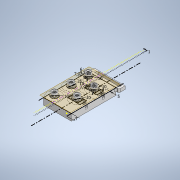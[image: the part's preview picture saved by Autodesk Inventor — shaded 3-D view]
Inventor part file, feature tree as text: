
AUTODESK INVENTOR PART (.ipt)
format: ipt  version: 2022.2 (Build 262287000, 287)  size: 5,227,520 bytes
history: native  units: mm
features: sketch x18, extrude x9, thread x5, revolve x5, helix x5, projected_geometry x4, other x3, plane x2, chamfer x1, reference x1
ambient origin geometry x8: Origin, YZ Plane, XZ Plane, XY Plane, X Axis, Y Axis, Z Axis, Center Point
bodies: Solid1 (feature_tree), Solid7 (feature_tree), Solid8 (feature_tree), Solid9 (feature_tree), Solid10 (feature_tree), Solid11 (feature_tree)
feature tree (53):
  sketch  "Sketch1"  dims[d0=20.0mm d1=7.92mm]
  extrude  "Base Plate"  Depth=7.92mm
  extrude  "Bearing Washer"  Depth=10.0mm
  extrude  "Straightening Pins"  Depth=1.0mm
  extrude  "Base Rails"  Depth=4.0mm
  extrude  "Slider Rails"  Depth=5.0mm
  extrude  "Nut Cavities"  Depth=10.0mm
  extrude  "Tightening Holes"  Depth=10.0mm
  extrude  "Spring Mount"  Depth=10.0mm
  chamfer  "Chamfer1"  Distance=10.0mm
  thread  "Thread1"  [1 undecoded]
  thread  "Thread2"  [1 undecoded]
  thread  "Thread3"  [1 undecoded]
  thread  "Thread4"  [1 undecoded]
  thread  "Thread5"  [1 undecoded]
  revolve  "Revolution6"  [1 undecoded]
  helix  "Coil6"  [1 undecoded]
  revolve  "Revolution7"  [1 undecoded]
  helix  "Coil7"  [1 undecoded]
  revolve  "Revolution8"  [1 undecoded]
  helix  "Coil8"  [1 undecoded]
  revolve  "Revolution9"  [1 undecoded]
  helix  "Coil9"  [1 undecoded]
  revolve  "Revolution10"  [1 undecoded]
  helix  "Coil10"  [1 undecoded]
  plane  "Work Plane3"
  sketch  "Sketch29"  dims[d188=0.7007mm d189=16.4mm d190=10.0mm d191=0.0mm d192=0.0mm d193=0.0mm d194=0.0mm d195=0.0mm]
  plane  "Work Plane4"
  extrude  "Extrusion13"  Depth=9.599311mm
  sketch  "Sketch30"  dims[d196=9.599311mm d197=0.112058mm d198=0.112058mm d201=0.7mm d203=9.599311mm d205=0.0mm d206=0.7007mm d207=16.4mm d208=10.0mm d209=0.0mm d210=0.0mm d211=0.0mm d212=0.0mm d213=0.0mm d214=9.599311mm d215=0.112058mm d216=0.112058mm d219=0.7mm d221=9.599311mm d223=0.0mm d224=0.7007mm d225=16.4mm d226=10.0mm d227=0.0mm d228=0.0mm d229=0.0mm d230=0.0mm d231=0.0mm d232=9.599311mm d233=0.112058mm d234=0.112058mm d237=0.7mm d239=9.599311mm d241=0.0mm d242=0.7007mm d243=16.4mm d244=10.0mm d245=0.0mm d246=0.0mm d247=0.0mm d248=0.0mm d249=0.0mm d250=9.599311mm d251=0.112058mm d252=0.112058mm d255=0.7mm d257=9.599311mm d259=0.0mm d260=0.7007mm d261=16.4mm d262=10.0mm d263=0.0mm d264=0.0mm d265=0.0mm d266=0.0mm d267=0.0mm d268=0.0mm d269=0.0mm d272=2.0mm d273=4.0mm]
  sketch  "Sketch2"  dims[d2=4.2mm d3=30.0mm d5=25.0mm d6=10.0mm d8=10.0mm]
  projected_geometry  "Projected Loop1"
  projected_geometry  "Projected Loop2"
  projected_geometry  "Projected Loop3"
  projected_geometry  "Projected Loop4"
  sketch  "Sketch3"  dims[d10=20.0mm d11=7.92mm d12=4.2mm d13=1.0mm]
  sketch  "Sketch4"  dims[d14=4.0mm d15=4.0mm]
  sketch  "Sketch5"  dims[d17=6.0mm d19=5.0mm]
  sketch  "Sketch6"  dims[d20=10.0mm d33=10.0mm]
  sketch  "Sketch19"  dims[d34=10.0mm d35=10.0mm]
  sketch  "Sketch20"  dims[d36=10.0mm d37=10.0mm d38=10.0mm d39=0.0mm d40=1.0mm d41=0.0mm d42=6.0mm d43=0.0mm d44=135.0deg d45=135.0deg d46=0.4mm]
  sketch  "Sketch21"  dims[d47=5.0mm d48=0.0mm d49=10.0mm d50=0.0mm d51=7.1mm]
  sketch  "Sketch22"  dims[d52=3.0mm d53=0.0mm d54=4.2mm d55=3.0mm d56=0.0mm]
  sketch  "Sketch23"  dims[d57=6.0mm d58=6.0mm d59=2.0mm d60=0.0mm d61=0.0mm]
  sketch  "Sketch24"  dims[d68=15.0mm d69=0.0mm d70=15.0mm d71=0.0mm d72=15.0mm d73=0.0mm d74=15.0mm d75=0.0mm d76=15.0mm d77=0.0mm d78=1.0mm d79=2.0mm d80=45.0deg d88=9.599311mm]
  sketch  "Sketch25"  dims[d106=9.599311mm d124=9.599311mm d142=9.599311mm]
  sketch  "Sketch26"  dims[d160=9.599311mm d171=7.0mm d178=9.599311mm d179=0.112058mm d180=0.112058mm]
  sketch  "Sketch27"  dims[d183=0.7mm d185=9.599311mm]
  sketch  "Sketch28"  dims[d187=0.0mm]
  reference  "Reference1"
  other  "<userpath>\Documents\Inventor\Wire Bender\Assembly.iam"
  other  "Assembly.iam"
  other  "Feed Motor Mount:1"
note: 15 required parameter values undecoded (feature->parameter linkage not recoverable at this tier; creation-order binding heuristic only, values carry confidence <= 0.55)